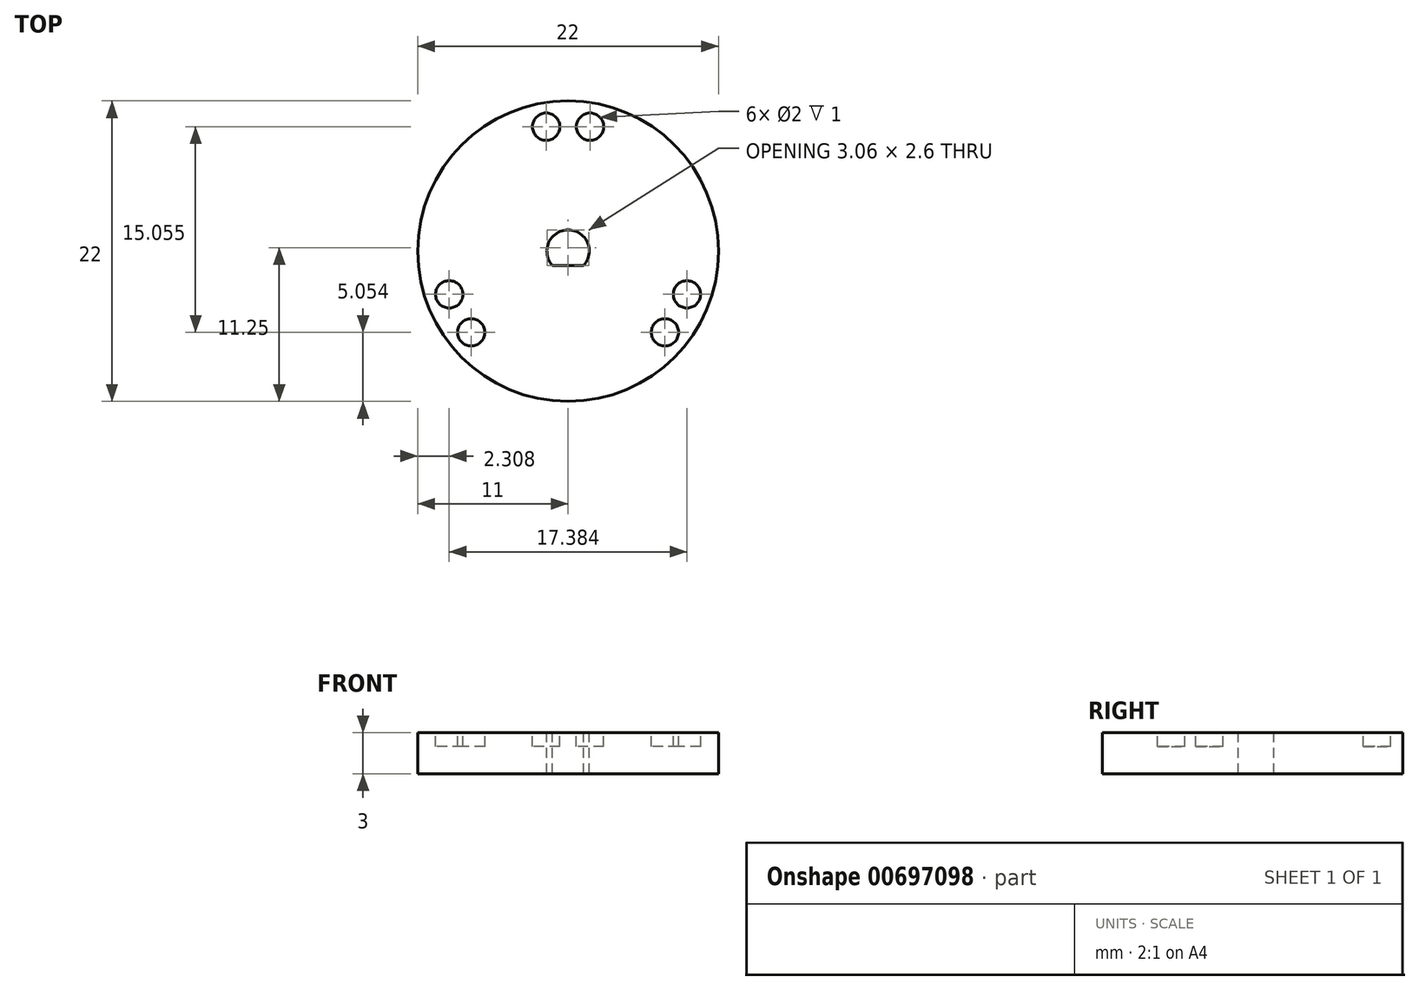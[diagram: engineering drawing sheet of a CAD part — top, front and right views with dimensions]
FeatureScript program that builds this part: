
annotation { "Feature Type Name" : "Feature", "Feature Type Description" : "" }
export const myFeature = defineFeature(function(context is Context, id is Id, definition is map)
    precondition{}
    {
        {
            var Q0;
            Q0=qCreatedBy(makeId("Top.planeOp"),FACE);
            var sketch = newSketch(context, id + "F0", { "sketchPlane" : qUnion([Q0])});
            skCircle(sketch, "E0", {"center": v(0, 0) * mm, "radius": 11 * mm});
            skSolve(sketch);
        }
        {
            var Q0;
            Q0 = qSketchRegion(id + "F0", true);
            extrude(context, id + "F1", {"entities" : qUnion([Q0]), "depth" : 3 * mm, "offsetDistance" : 25 * mm});
        }
        {
            var Q0;
            Q0=makeQuery(id+"F1.opExtrude","CAP_FACE",FACE,{"disambiguationData":[OSD([sQuery(id+"F0.wireOp",EDGE,"E0")])],"isStart":false});
            var sketch = newSketch(context, id + "F2", { "sketchPlane" : qUnion([Q0])});
            skCircle(sketch, "E1", {"center": v(0, 0) * mm, "radius": 1.55 * mm, "construction": true});
            skLineSegment(sketch, "E2", {"start": v(-1.14, -1.05) * mm, "end": v(1.14, -1.05) * mm});
            skLineSegment(sketch, "E3", {"start": v(0, 1.55) * mm, "end": v(0, -1.05) * mm, "construction": true});
            skArc(sketch, "E4", {"start": v(1.14, -1.05) * mm, "mid": v(0, 1.55) * mm, "end": v(-1.14, -1.05) * mm});
            skSolve(sketch);
        }
        {
            var Q0;
            Q0 = qSketchRegion(id + "F2", true);
            extrude(context, id + "F3", {"entities" : qUnion([Q0]), "operationType" : NewBodyOperationType.REMOVE, "oppositeDirection" : true, "depth" : 3 * mm, "offsetDistance" : 25 * mm});
        }
        {
            var Q0;
            Q0=makeQuery(id+"F1.opExtrude","CAP_FACE",FACE,{"disambiguationData":[OSD([sQuery(id+"F0.wireOp",EDGE,"E0")])],"isStart":false});
            var sketch = newSketch(context, id + "F4", { "sketchPlane" : qUnion([Q0])});
            skCircle(sketch, "E5", {"center": v(0, 0) * mm, "radius": 9.25 * mm, "construction": true});
            skLineSegment(sketch, "E6", {"start": v(0, 0) * mm, "end": v(0, 9.25) * mm, "construction": true});
            skLineSegment(sketch, "E7", {"start": v(0, 0) * mm, "end": v(8.01, -4.62) * mm, "construction": true});
            skLineSegment(sketch, "E8", {"start": v(0, 0) * mm, "end": v(-8.01, -4.62) * mm, "construction": true});
            skCircle(sketch, "E9", {"center": v(-1.6, 9.1) * mm, "radius": 1 * mm});
            skCircle(sketch, "E10", {"center": v(-7.09, -5.95) * mm, "radius": 1 * mm});
            skLineSegment(sketch, "E11", {"start": v(0, 0) * mm, "end": v(-1.6, 9.1) * mm, "construction": true});
            skLineSegment(sketch, "E12", {"start": v(0, 0) * mm, "end": v(1.6, 9.1) * mm, "construction": true});
            skCircle(sketch, "E13", {"center": v(1.6, 9.1) * mm, "radius": 1 * mm});
            skLineSegment(sketch, "E14", {"start": v(0, 0) * mm, "end": v(-8.7, -3.16) * mm, "construction": true});
            skLineSegment(sketch, "E15", {"start": v(0, 0) * mm, "end": v(-7.09, -5.95) * mm, "construction": true});
            skCircle(sketch, "E16", {"center": v(-8.7, -3.16) * mm, "radius": 1 * mm});
            skLineSegment(sketch, "E17", {"start": v(0, 0) * mm, "end": v(8.7, -3.16) * mm, "construction": true});
            skLineSegment(sketch, "E18", {"start": v(0, 0) * mm, "end": v(7.09, -5.95) * mm, "construction": true});
            skCircle(sketch, "E19", {"center": v(8.7, -3.16) * mm, "radius": 1 * mm});
            skCircle(sketch, "E20", {"center": v(7.09, -5.95) * mm, "radius": 1 * mm});
            skSolve(sketch);
        }
        {
            var Q0;
            Q0 = qSketchRegion(id + "F4", true);
            extrude(context, id + "F5", {"entities" : qUnion([Q0]), "operationType" : NewBodyOperationType.REMOVE, "oppositeDirection" : true, "depth" : 1 * mm, "offsetDistance" : 25 * mm});
        }
    });
